# Revit family: Shower_Arm_Bracket-American_Standard-Spectra-8888096_Series
name_source: partatom
category: Plumbing Fixtures
units: mm (PartAtom-declared; Revit-internal decimal feet)

## family parameters
Cut with Voids When Loaded = No
Host = Face
OmniClass Number = 23.45.05.14.17
OmniClass Title = Showers
Part Type = Normal
Room Calculation Point = No
Round Connector Dimension = Use Diameter
Shared = Yes

## types (5) — shared parameters
Assembly Code = D2020300
CW Connection = No
CWFU = 3
Default Elevation = 72"
Description = Shower Arm Bracket
HW Connection = No
HWFU = 3
Installation Type = Attaches to shower arm.
Length = 3 9/16"
Manufacturer = American Standard
Price = Prices may vary. Please consult Manufacturer Representative for most up-to-date price list.
Product Documentation Link = https://americanstandard.box.com
Product Page URL = https://www.americanstandard-us.com
Revised Date = 08/04/2022
Tempered Water Connection = Yes
Tempered Water Connection Diameter = 1/2"
Tempered Water Connection Radius = 1/4"
URL = https://www.americanstandard-us.com
Vent Connection = No
WFU = 4
Warranty Information = One Year General Product Warranty
Waste Connection = No
Width = 2 7/16"

## per-type parameters (varying)
| type | Finish | Material |
| 8888096.002 | Metal-American Standard-002-Polished Chrome | Metal-American Standard-002-Polished Chrome |
| 8888096.243 | Metal-American Standard-243-Matte Black | Metal-American Standard-243-Matte Black |
| 8888096.278 | Metal-American Standard-278-Legacy Bronze | Metal-American Standard-278-Legacy Bronze |
| 8888096.013 | Metal-American Standard-013-Polished Nickel PVD | Metal-American Standard-013-Polished Nickel PVD |
| 8888096.295 | Metal-American Standard-295-Brushed Nickel | Metal-American Standard-295-Brushed Nickel |

note: column(s) folded — value = type name in every type: Model

## geometry (parser evidence)
native form markers: Sweep x3
no freeform markers — native parametric forms only
